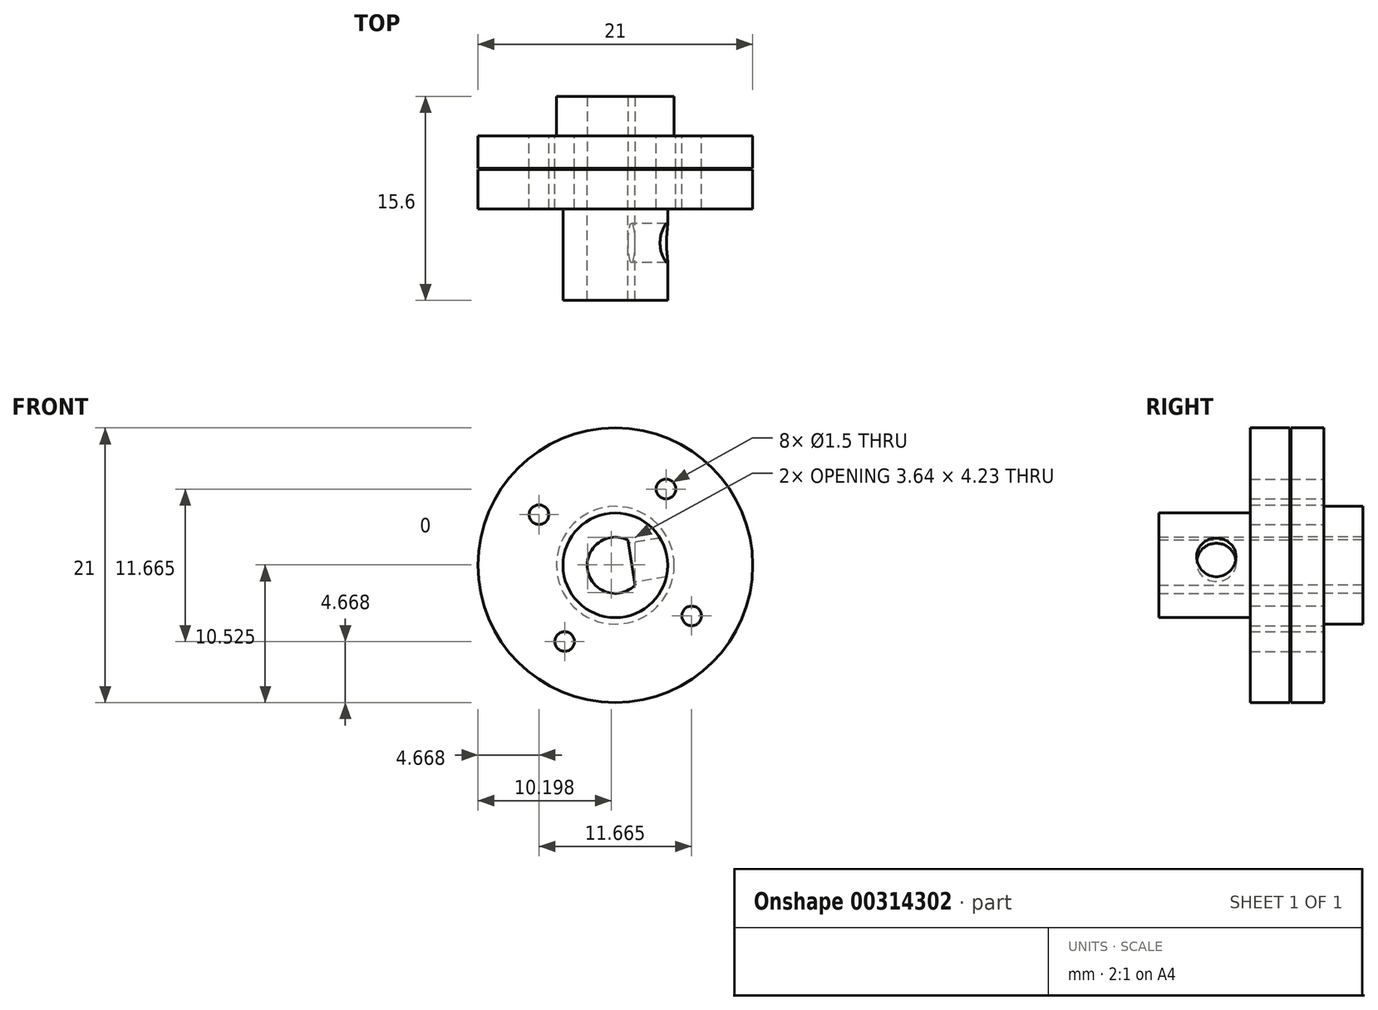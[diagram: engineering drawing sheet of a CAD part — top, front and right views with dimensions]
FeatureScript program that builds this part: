
annotation { "Feature Type Name" : "Feature", "Feature Type Description" : "" }
export const myFeature = defineFeature(function(context is Context, id is Id, definition is map)
    precondition{}
    {
        {
            var Q0;
            Q0=qCreatedBy(makeId("Front.planeOp"),FACE);
            var sketch = newSketch(context, id + "F0", { "sketchPlane" : qUnion([Q0]), "asVersion" : FeatureScriptVersionNumber.V442_PARTING_OUT_TARGET_READONLY});
            skCircle(sketch, "E0", {"center": v(0, 0) * mm, "radius": 10.5 * mm});
            skCircle(sketch, "E1", {"center": v(0, 0) * mm, "radius": 4.5 * mm});
            skLineSegment(sketch, "E2", {"start": v(0, 0) * mm, "end": v(8.75, -5.8) * mm, "construction": true});
            skLineSegment(sketch, "E3", {"start": v(0, 0) * mm, "end": v(-8.75, 5.8) * mm, "construction": true});
            skLineSegment(sketch, "E4", {"start": v(0, 0) * mm, "end": v(5.8, 8.75) * mm, "construction": true});
            skLineSegment(sketch, "E5", {"start": v(0, 0) * mm, "end": v(-5.8, -8.75) * mm, "construction": true});
            skCircle(sketch, "E6", {"center": v(-5.83, 3.87) * mm, "radius": 0.75 * mm});
            skCircle(sketch, "E7", {"center": v(3.87, 5.83) * mm, "radius": 0.75 * mm});
            skCircle(sketch, "E8", {"center": v(5.83, -3.87) * mm, "radius": 0.75 * mm});
            skCircle(sketch, "E9", {"center": v(-3.87, -5.83) * mm, "radius": 0.75 * mm});
            skSolve(sketch);
        }
        {
            var Q0;
            Q0=makeQuery(id+"F0.imprint","IMPRINT",FACE,{"disambiguationData":[TD([[makeQuery(id+"F0.imprint","IMPRINT",EDGE,{"derivedFrom":sQuery(id+"F0.wireOp",EDGE,"E0")}),1.0]])]});
            var Q1;
            Q1=makeQuery(id+"F0.imprint","IMPRINT",FACE,{"disambiguationData":[TD([[makeQuery(id+"F0.imprint","IMPRINT",EDGE,{"derivedFrom":sQuery(id+"F0.wireOp",EDGE,"E1")}),1.0]])]});
            extrude(context, id + "F1", {"entities" : qUnion([Q0, Q1]), "depth" : 2.5 * mm});
        }
        {
            var Q0;
            Q0=makeQuery(id+"F0.imprint","IMPRINT",FACE,{"disambiguationData":[TD([[makeQuery(id+"F0.imprint","IMPRINT",EDGE,{"derivedFrom":sQuery(id+"F0.wireOp",EDGE,"E1")}),1.0]])]});
            extrude(context, id + "F2", {"entities" : qUnion([Q0]), "operationType" : NewBodyOperationType.ADD, "oppositeDirection" : true, "depth" : (5.5 - 2.5) * mm});
        }
        {
            var Q0;
            Q0=makeQuery(id+"F1.opExtrude","CAP_FACE",FACE,{"disambiguationData":[OSD([sQuery(id+"F0.wireOp",EDGE,"E0"),sQuery(id+"F0.wireOp",EDGE,"E6"),sQuery(id+"F0.wireOp",EDGE,"E7"),sQuery(id+"F0.wireOp",EDGE,"E8"),sQuery(id+"F0.wireOp",EDGE,"E9")])],"isStart":false});
            var sketch = newSketch(context, id + "F3", { "sketchPlane" : qUnion([Q0]), "asVersion" : FeatureScriptVersionNumber.V442_PARTING_OUT_TARGET_READONLY});
            skCircle(sketch, "E10.0.0", {"center": v(0, 0) * mm, "radius": 10.5 * mm});
            skCircle(sketch, "E11.0", {"center": v(3.87, 5.83) * mm, "radius": 0.75 * mm});
            skCircle(sketch, "E12.0", {"center": v(-5.83, 3.87) * mm, "radius": 0.75 * mm});
            skCircle(sketch, "E13.0", {"center": v(-3.87, -5.83) * mm, "radius": 0.75 * mm});
            skCircle(sketch, "E14.0", {"center": v(5.83, -3.87) * mm, "radius": 0.75 * mm});
            skSolve(sketch);
        }
        {
            var Q0;
            Q0=makeQuery(id+"F3.imprint","IMPRINT",FACE,{"disambiguationData":[TD([[makeQuery(id+"F3.imprint","IMPRINT",EDGE,{"derivedFrom":sQuery(id+"F3.wireOp",EDGE,"E10.0.0")}),1.0]])]});
            extrude(context, id + "F4", {"entities" : qUnion([Q0]), "depth" : 3.1 * mm, "hasSecondDirection" : true, "secondDirectionOppositeDirection" : false, "secondDirectionDepth" : 0.1 * mm});
        }
        {
            var Q0;
            Q0=makeQuery(id+"F4.opExtrude","CAP_FACE",FACE,{"disambiguationData":[OSD([sQuery(id+"F3.wireOp",EDGE,"E10.0.0"),sQuery(id+"F3.wireOp",EDGE,"E11.0"),sQuery(id+"F3.wireOp",EDGE,"E12.0"),sQuery(id+"F3.wireOp",EDGE,"E13.0"),sQuery(id+"F3.wireOp",EDGE,"E14.0")])],"isStart":false});
            var sketch = newSketch(context, id + "F5", { "sketchPlane" : qUnion([Q0]), "asVersion" : FeatureScriptVersionNumber.V442_PARTING_OUT_TARGET_READONLY});
            skCircle(sketch, "E15.0.0", {"center": v(0, 0) * mm, "radius": 10.5 * mm});
            skCircle(sketch, "E16", {"center": v(0, 0) * mm, "radius": 4 * mm});
            skCircle(sketch, "E17", {"center": v(0, 0) * mm, "radius": 2.15 * mm});
            skLineSegment(sketch, "E18", {"start": v(0.95, 1.93) * mm, "end": v(1.52, -1.52) * mm});
            skSolve(sketch);
        }
        {
            var Q0;
            {var subQ0=sQuery(id+"F5.wireOp",EDGE,"E18");Q0=makeQuery(id+"F5.imprint","IMPRINT",FACE,{"disambiguationData":[TD([[makeQuery(id+"F5.imprint","IMPRINT",EDGE,{"derivedFrom":subQ0}),1.0]])]});}
            var Q1;
            Q1=makeQuery(id+"F5.imprint","IMPRINT",FACE,{"disambiguationData":[TD([[makeQuery(id+"F5.imprint","IMPRINT",EDGE,{"derivedFrom":sQuery(id+"F5.wireOp",EDGE,"E16")}),1.0]])]});
            extrude(context, id + "F6", {"entities" : qUnion([Q0, Q1]), "operationType" : NewBodyOperationType.ADD, "depth" : 7 * mm});
        }
        {
            var Q0;
            Q0=makeQuery(id+"F6.boolean.opBoolean","SPLIT",FACE,{"disambiguationData":[TD([makeQuery(id+"F6.opExtrude","SWEPT_FACE",FACE,{"disambiguationData":[OSD([sQuery(id+"F5.wireOp",EDGE,"E17")])]})])],"derivedFrom":makeQuery(id+"F4.opExtrude","CAP_FACE",FACE,{"disambiguationData":[OSD([sQuery(id+"F3.wireOp",EDGE,"E10.0.0"),sQuery(id+"F3.wireOp",EDGE,"E11.0"),sQuery(id+"F3.wireOp",EDGE,"E12.0"),sQuery(id+"F3.wireOp",EDGE,"E13.0"),sQuery(id+"F3.wireOp",EDGE,"E14.0")])],"isStart":false})});
            extrude(context, id + "F7", {"entities" : qUnion([Q0]), "operationType" : NewBodyOperationType.REMOVE, "oppositeDirection" : true, "depth" : 25 * mm});
        }
        {
            var Q0;
            {var subQ0=sQuery(id+"F5.wireOp",EDGE,"E18");Q0=makeQuery(id+"F7.boolean.opBoolean","MERGE",FACE,{"derivedFrom":[makeQuery(id+"F6.opExtrude","SWEPT_FACE",FACE,{"disambiguationData":[OSD([subQ0])]}),makeQuery(id+"F7.opExtrude","SWEPT_FACE",FACE,{"disambiguationData":[OSD([subQ0])]})]});}
            var sketch = newSketch(context, id + "F8", { "sketchPlane" : qUnion([Q0]), "asVersion" : FeatureScriptVersionNumber.V442_PARTING_OUT_TARGET_READONLY});
            skLineSegment(sketch, "E19.0.0", {"start": v(12.6, 1.75) * mm, "end": v(2.6, 1.75) * mm});
            skLineSegment(sketch, "E19.0.1", {"start": v(2.6, 1.75) * mm, "end": v(2.6, -1.75) * mm});
            skLineSegment(sketch, "E19.0.2", {"start": v(2.6, -1.75) * mm, "end": v(12.6, -1.75) * mm});
            skLineSegment(sketch, "E19.0.3", {"start": v(12.6, -1.75) * mm, "end": v(12.6, 1.75) * mm});
            skLineSegment(sketch, "E20.0", {"start": v(5.6, 10.5) * mm, "end": v(5.6, -10.5) * mm});
            skLineSegment(sketch, "E21", {"start": v(8.2, 1.75) * mm, "end": v(8.2, -1.75) * mm, "construction": true});
            skPoint(sketch, "E21.endSnap0", {"position": v(7.6, -1.75) * mm});
            skCircle(sketch, "E22", {"center": v(8.2, 0) * mm, "radius": 1.5 * mm});
            skSolve(sketch);
        }
        {
            var Q0;
            Q0=makeQuery(id+"F8.imprint","IMPRINT",FACE,{"disambiguationData":[TD([[makeQuery(id+"F8.imprint","IMPRINT",EDGE,{"derivedFrom":sQuery(id+"F8.wireOp",EDGE,"E22")}),1.0]])]});
            extrude(context, id + "F9", {"entities" : qUnion([Q0]), "operationType" : NewBodyOperationType.REMOVE, "oppositeDirection" : true, "depth" : 2.8 * mm});
        }
    });
